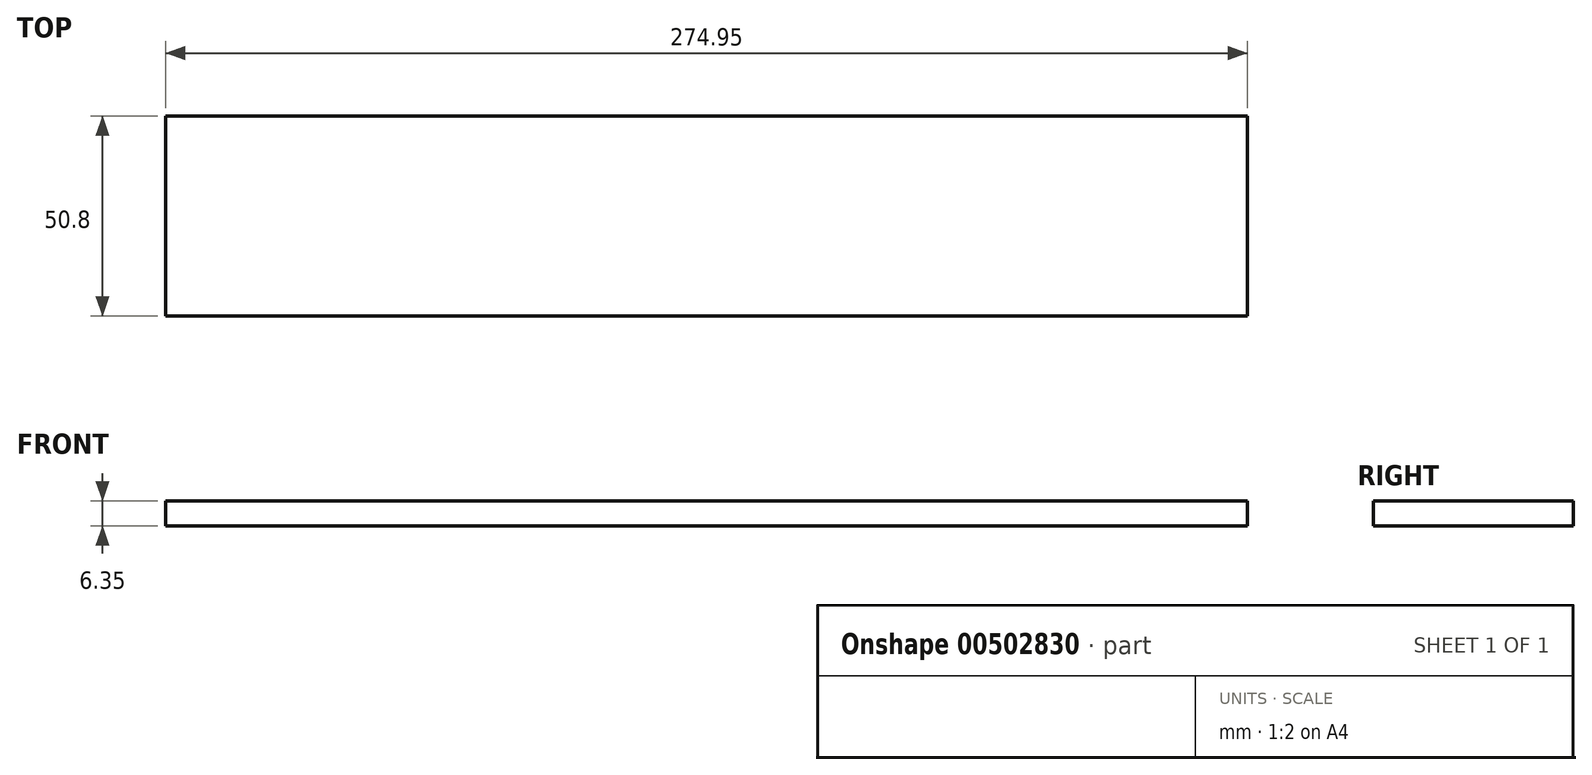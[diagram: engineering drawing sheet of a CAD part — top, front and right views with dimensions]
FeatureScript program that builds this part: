
annotation { "Feature Type Name" : "Feature", "Feature Type Description" : "" }
export const myFeature = defineFeature(function(context is Context, id is Id, definition is map)
    precondition{}
    {
        {
            var Q0;
            Q0=qCreatedBy(makeId("Top.planeOp"),FACE);
            var sketch = newSketch(context, id + "F0", { "sketchPlane" : qUnion([Q0])});
            skLineSegment(sketch, "E0.bottom", {"start": v(0, 0) * mm, "end": v(274.95, 0) * mm});
            skLineSegment(sketch, "E0.top", {"start": v(0, -50.8) * mm, "end": v(274.95, -50.8) * mm});
            skLineSegment(sketch, "E0.left", {"start": v(0, 0) * mm, "end": v(0, -50.8) * mm});
            skLineSegment(sketch, "E0.right", {"start": v(274.95, 0) * mm, "end": v(274.95, -50.8) * mm});
            skSolve(sketch);
        }
        {
            var Q0;
            Q0=makeQuery(id+"F0.imprint","IMPRINT",FACE,{"disambiguationData":[TD([[makeQuery(id+"F0.imprint","IMPRINT",EDGE,{"derivedFrom":sQuery(id+"F0.wireOp",EDGE,"E0.bottom")}),-1.0]])]});
            extrude(context, id + "F1", {"entities" : qUnion([Q0]), "depth" : 6.35 * mm, "offsetDistance" : 25.4 * mm});
        }
    });
